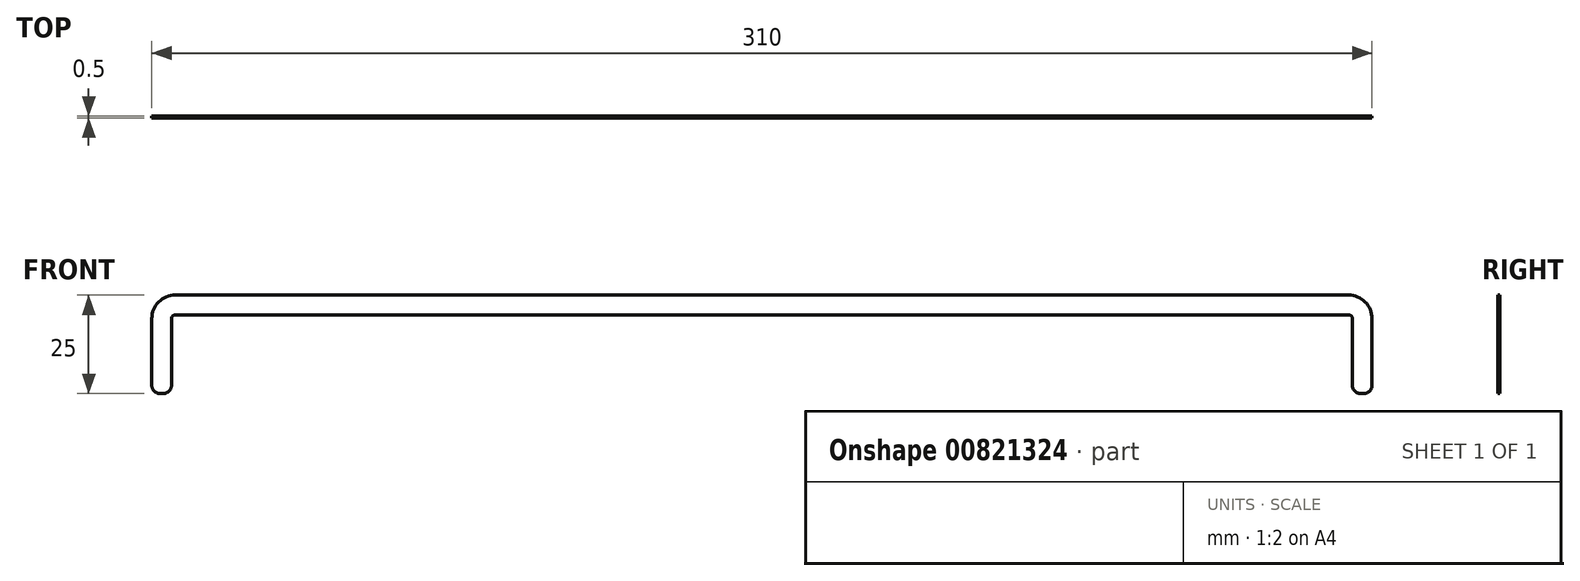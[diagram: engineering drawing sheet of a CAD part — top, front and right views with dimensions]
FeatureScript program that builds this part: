
annotation { "Feature Type Name" : "Feature", "Feature Type Description" : "" }
export const myFeature = defineFeature(function(context is Context, id is Id, definition is map)
    precondition{}
    {
        {
            var Q0;
            Q0=qCreatedBy(makeId("Front.planeOp"),FACE);
            var sketch = newSketch(context, id + "F0", { "sketchPlane" : qUnion([Q0])});
            skLineSegment(sketch, "E0", {"start": v(-148.9, -2.8) * mm, "end": v(-148.9, 14.2) * mm});
            skLineSegment(sketch, "E1", {"start": v(-147.9, 15.2) * mm, "end": v(150.1, 15.2) * mm});
            skLineSegment(sketch, "E2", {"start": v(151.1, 14.2) * mm, "end": v(151.1, -2.8) * mm});
            skLineSegment(sketch, "E3", {"start": v(153.1, -4.8) * mm, "end": v(154.1, -4.8) * mm});
            skLineSegment(sketch, "E4", {"start": v(156.1, -2.8) * mm, "end": v(156.1, 14.2) * mm});
            skLineSegment(sketch, "E5", {"start": v(150.1, 20.2) * mm, "end": v(-147.9, 20.2) * mm});
            skLineSegment(sketch, "E6", {"start": v(-153.9, 14.2) * mm, "end": v(-153.9, -2.8) * mm});
            skLineSegment(sketch, "E7", {"start": v(-151.9, -4.8) * mm, "end": v(-150.9, -4.8) * mm});
            skPoint(sketch, "E8.visualSharp", {"position": v(-148.9, 15.2) * mm});
            skArc(sketch, "E8.filletArc", {"start": v(-147.9, 15.2) * mm, "mid": v(-148.6, 14.9) * mm, "end": v(-148.9, 14.2) * mm});
            skPoint(sketch, "E9.visualSharp", {"position": v(151.1, 15.2) * mm});
            skArc(sketch, "E9.filletArc", {"start": v(151.1, 14.2) * mm, "mid": v(150.8, 14.9) * mm, "end": v(150.1, 15.2) * mm});
            skPoint(sketch, "E10.visualSharp", {"position": v(156.1, 20.2) * mm});
            skArc(sketch, "E10.filletArc", {"start": v(156.1, 14.2) * mm, "mid": v(154.34, 18.44) * mm, "end": v(150.1, 20.2) * mm});
            skPoint(sketch, "E11.visualSharp", {"position": v(-153.9, 20.2) * mm});
            skArc(sketch, "E11.filletArc", {"start": v(-147.9, 20.2) * mm, "mid": v(-152.14, 18.44) * mm, "end": v(-153.9, 14.2) * mm});
            skPoint(sketch, "E12.visualSharp", {"position": v(-148.9, -4.8) * mm});
            skArc(sketch, "E12.filletArc", {"start": v(-150.9, -4.8) * mm, "mid": v(-149.48, -4.21) * mm, "end": v(-148.9, -2.8) * mm});
            skPoint(sketch, "E13.visualSharp", {"position": v(-153.9, -4.8) * mm});
            skArc(sketch, "E13.filletArc", {"start": v(-153.9, -2.8) * mm, "mid": v(-153.31, -4.21) * mm, "end": v(-151.9, -4.8) * mm});
            skPoint(sketch, "E14.visualSharp", {"position": v(151.1, -4.8) * mm});
            skArc(sketch, "E14.filletArc", {"start": v(151.1, -2.8) * mm, "mid": v(151.69, -4.21) * mm, "end": v(153.1, -4.8) * mm});
            skPoint(sketch, "E15.visualSharp", {"position": v(156.1, -4.8) * mm});
            skArc(sketch, "E15.filletArc", {"start": v(154.1, -4.8) * mm, "mid": v(155.52, -4.21) * mm, "end": v(156.1, -2.8) * mm});
            skSolve(sketch);
        }
        {
            var Q0;
            Q0 = qSketchRegion(id + "F0", true);
            extrude(context, id + "F1", {"entities" : qUnion([Q0]), "depth" : .5 * mm, "offsetDistance" : 25 * mm});
        }
    });
